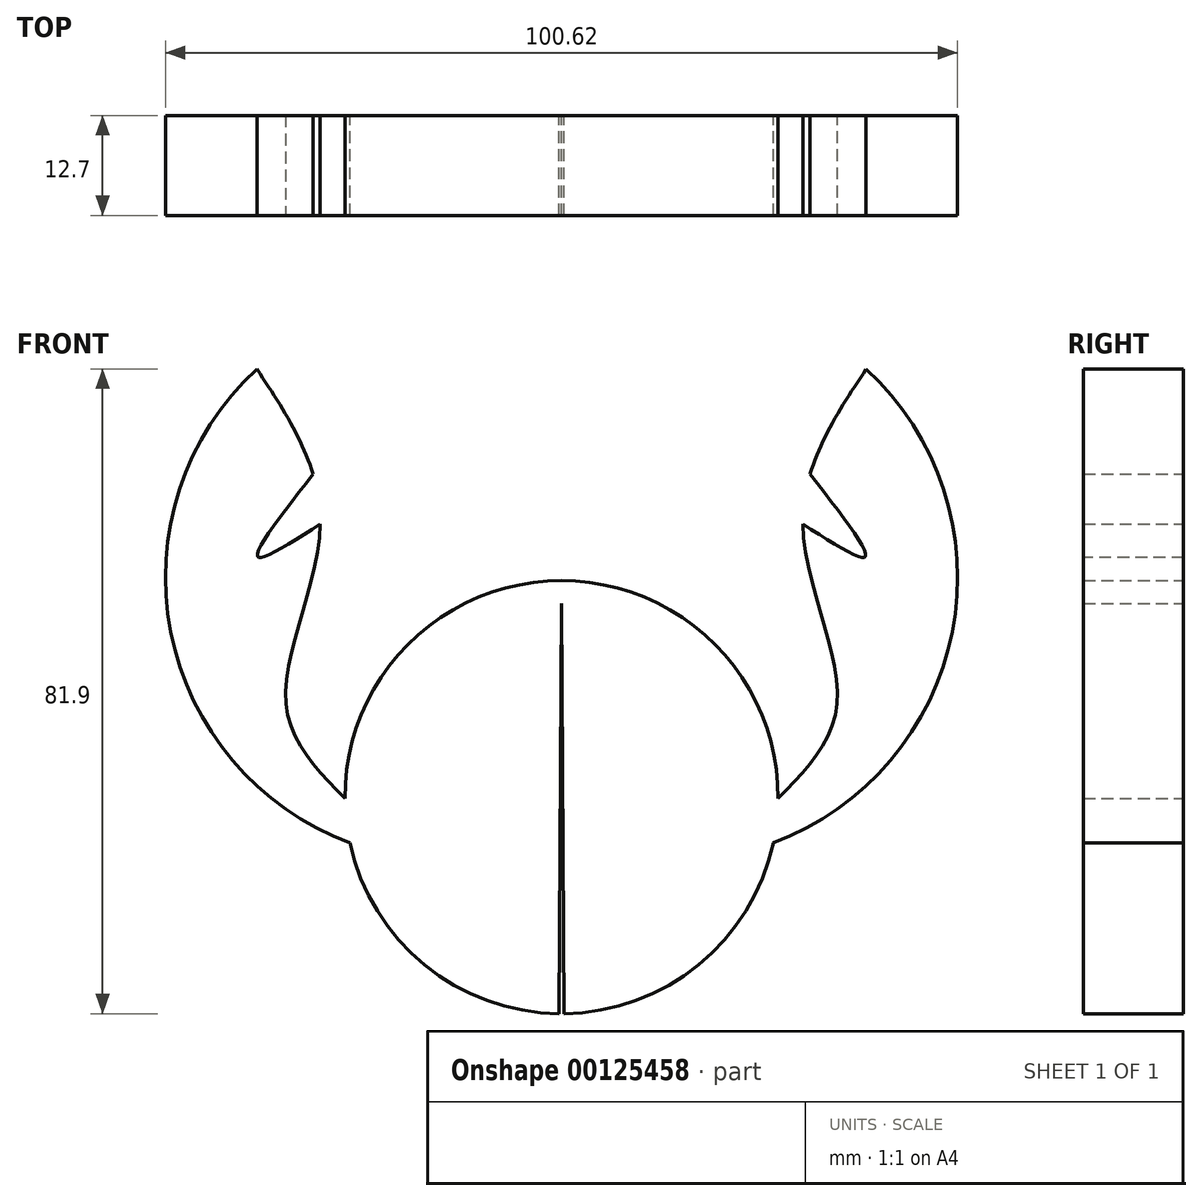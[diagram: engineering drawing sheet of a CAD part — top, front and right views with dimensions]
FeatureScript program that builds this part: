
annotation { "Feature Type Name" : "Feature", "Feature Type Description" : "" }
export const myFeature = defineFeature(function(context is Context, id is Id, definition is map)
    precondition{}
    {
        {
            var Q0;
            Q0=qCreatedBy(makeId("Front.planeOp"),FACE);
            var sketch = newSketch(context, id + "F0", { "sketchPlane" : qUnion([Q0])});
            skArc(sketch, "E0", {"start": v(-38.7, 54.4) * mm, "mid": v(-49.64, 21) * mm, "end": v(-26.89, -5.8) * mm});
            skArc(sketch, "E1", {"start": v(0.02, 27.5) * mm, "mid": v(-19.5, 19.4) * mm, "end": v(-27.5, -0.15) * mm});
            skPoint(sketch, "E2.3.internal.snap0", {"position": v(-27.5, 0.15) * mm});
            skFitSpline(sketch, "E2", {"points": [v(-38.7, 54.4) * mm, v(-30.65, 34.71) * mm, v(-35, 12.09) * mm, v(-27.5, -0.15) * mm], "startDerivative": vector(35.09, -53.36) * mm, "endDerivative": vector(37.31, -37.64) * mm});
            skArc(sketch, "E3.trimOffspring", {"start": v(-26.89, -5.8) * mm, "mid": v(-17.4, -21.3) * mm, "end": v(-0.29, -27.5) * mm});
            skPoint(sketch, "E4.orphan", {"position": v(-0.02, 27.5) * mm});
            skFitSpline(sketch, "E5", {"points": [v(-31.57, 41.03) * mm, v(-38.58, 30.54) * mm, v(-30.65, 34.71) * mm], "startDerivative": vector(-21, -27.03) * mm, "endDerivative": vector(24.23, 15.63) * mm});
            skFitSpline(sketch, "E6.trimOffspring", {"points": [v(-38.7, 54.4) * mm, v(-30.65, 34.71) * mm, v(-35, 12.09) * mm, v(-27.5, -0.15) * mm], "startDerivative": vector(35.09, -53.36) * mm, "endDerivative": vector(37.31, -37.64) * mm});
            skPoint(sketch, "E7.MirrorP", {"position": v(0.02, 27.5) * mm});
            skLineSegment(sketch, "E8", {"start": v(0.02, 27.5) * mm, "end": v(-0.29, -27.5) * mm});
            skSolve(sketch);
        }
        {
            var Q0;
            Q0=makeQuery(id+"F0.imprint","IMPRINT",FACE,{"disambiguationData":[TD([[makeQuery(id+"F0.imprint","IMPRINT",EDGE,{"derivedFrom":sQuery(id+"F0.wireOp",EDGE,"E0")}),1.0]])]});
            extrude(context, id + "F1", {"entities" : qUnion([Q0]), "depth" : 12.7 * mm});
        }
        {
            var Q0;
            Q0=makeQuery(id+"F1.opExtrude","SWEPT_BODY",BODY,{"disambiguationData":[OSD([sQuery(id+"F0.wireOp",EDGE,"E0"),sQuery(id+"F0.wireOp",EDGE,"E1"),sQuery(id+"F0.wireOp",EDGE,"E2"),sQuery(id+"F0.wireOp",EDGE,"E3.trimOffspring"),sQuery(id+"F0.wireOp",EDGE,"E5"),sQuery(id+"F0.wireOp",EDGE,"E6.trimOffspring"),sQuery(id+"F0.wireOp",EDGE,"E8")])]});
            var Q1;
            Q1=qCreatedBy(makeId("Right.planeOp"),FACE);
            mirror(context, id + "F2", {"operationType" : NewBodyOperationType.ADD, "entities" : qUnion([Q0]), "mirrorPlane" : qUnion([Q1])});
        }
    });
